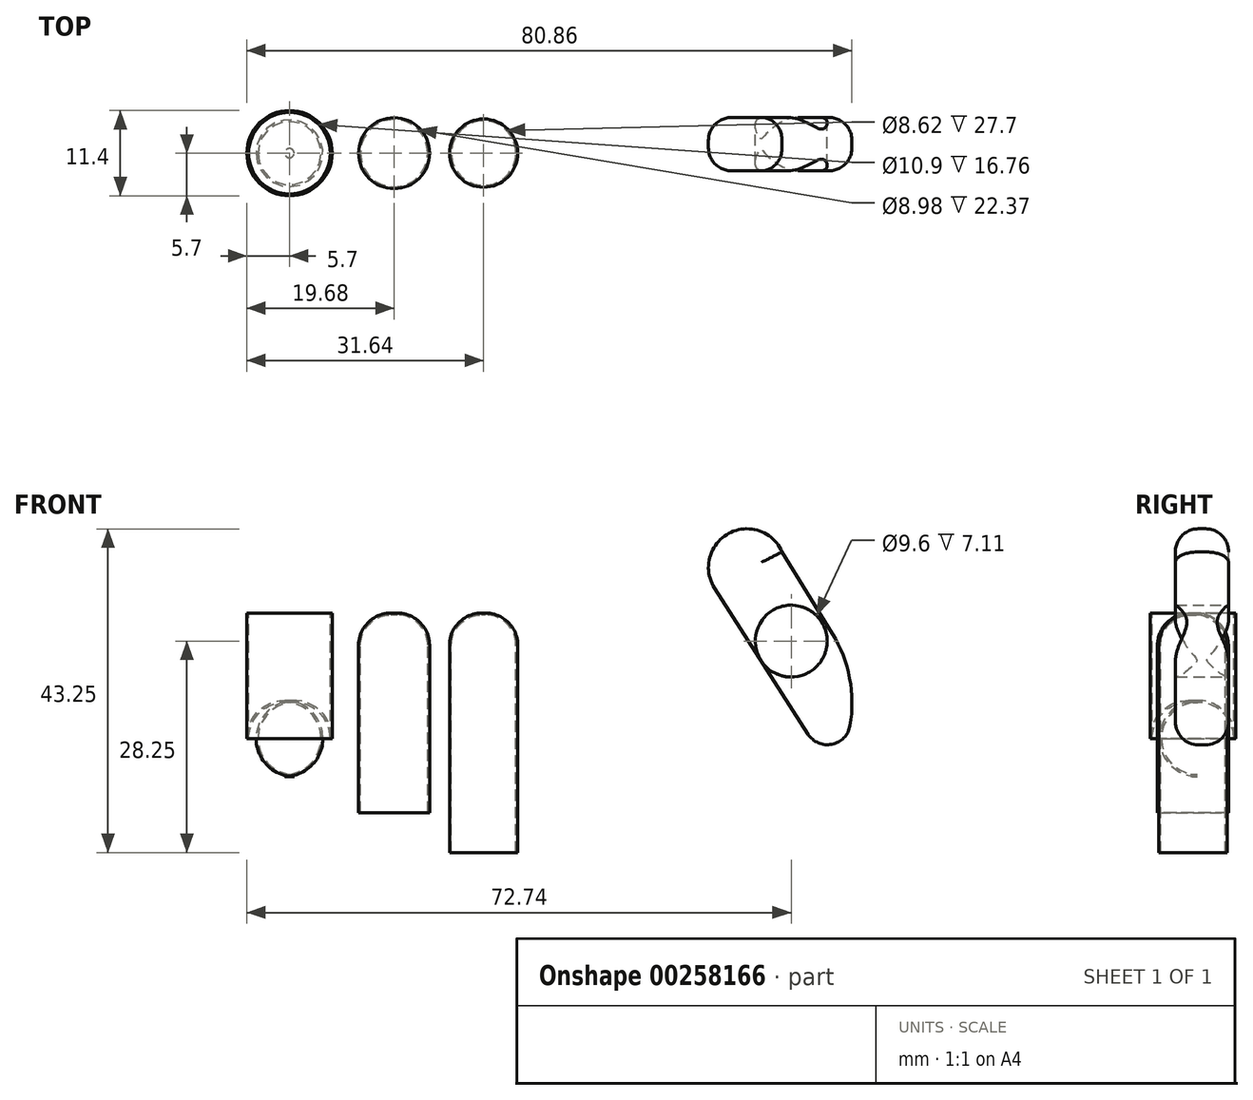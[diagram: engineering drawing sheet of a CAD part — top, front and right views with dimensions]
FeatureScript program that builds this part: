
annotation { "Feature Type Name" : "Feature", "Feature Type Description" : "" }
export const myFeature = defineFeature(function(context is Context, id is Id, definition is map)
    precondition{}
    {
        {
            var Q0;
            Q0=qCreatedBy(makeId("Front.planeOp"),FACE);
            var sketch = newSketch(context, id + "F0", { "sketchPlane" : qUnion([Q0])});
            skLineSegment(sketch, "E0", {"start": v(-7.79, 3.36) * mm, "end": v(7.96, -21.27) * mm});
            skLineSegment(sketch, "E1", {"start": v(7.96, -2.76) * mm, "end": v(1.24, 8.17) * mm});
            skArc(sketch, "E2", {"start": v(-7.79, 3.36) * mm, "mid": v(-5.88, 10.65) * mm, "end": v(1.24, 8.17) * mm});
            skCircle(sketch, "E3", {"center": v(2.46, -3.75) * mm, "radius": 4.8 * mm});
            skLineSegment(sketch, "E4", {"start": v(2.46, -3.75) * mm, "end": v(-1.63, -6.27) * mm});
            skLineSegment(sketch, "E5", {"start": v(-1.63, -6.27) * mm, "end": v(2.46, -3.75) * mm});
            skLineSegment(sketch, "E6", {"start": v(2.46, -3.75) * mm, "end": v(6.56, -1.23) * mm});
            skArc(sketch, "E7", {"start": v(7.96, -2.76) * mm, "mid": v(10.58, -12.01) * mm, "end": v(7.96, -21.27) * mm});
            skSolve(sketch);
        }
        {
            var Q0;
            {var subQ0=sQuery(id+"F0.wireOp",EDGE,"E5");Q0=makeQuery(id+"F0.imprint","IMPRINT",FACE,{"disambiguationData":[TD([[makeQuery(id+"F0.imprint","IMPRINT",EDGE,{"derivedFrom":subQ0}),-1.0]])]});}
            var Q1;
            {var subQ0=sQuery(id+"F0.wireOp",EDGE,"E5");Q1=makeQuery(id+"F0.imprint","IMPRINT",FACE,{"disambiguationData":[TD([[makeQuery(id+"F0.imprint","IMPRINT",EDGE,{"derivedFrom":subQ0}),1.0]])]});}
            var Q2;
            Q2=makeQuery(id+"F0.imprint","IMPRINT",FACE,{"disambiguationData":[TD([[makeQuery(id+"F0.imprint","IMPRINT",EDGE,{"derivedFrom":sQuery(id+"F0.wireOp",EDGE,"E1")}),1.0]])]});
            extrude(context, id + "F1", {"entities" : qUnion([Q0, Q1, Q2]), "depth" : 7.11 * mm});
        }
        {
            var Q0;
            Q0=makeQuery(id+"F1.opExtrude","CAP_EDGE",EDGE,{"disambiguationData":[OSD([sQuery(id+"F0.wireOp",EDGE,"E0")])],"isStart":true});
            var Q1;
            Q1=makeQuery(id+"F1.opExtrude","CAP_EDGE",EDGE,{"disambiguationData":[OSD([sQuery(id+"F0.wireOp",EDGE,"E2")])],"isStart":true});
            var Q2;
            Q2=makeQuery(id+"F1.opExtrude","CAP_EDGE",EDGE,{"disambiguationData":[OSD([sQuery(id+"F0.wireOp",EDGE,"E2")])],"isStart":false});
            var Q3;
            Q3=makeQuery(id+"F1.opExtrude","CAP_EDGE",EDGE,{"disambiguationData":[OSD([sQuery(id+"F0.wireOp",EDGE,"E0")])],"isStart":false});
            var Q4;
            Q4=makeQuery(id+"F1.opExtrude","CAP_EDGE",EDGE,{"disambiguationData":[OSD([sQuery(id+"F0.wireOp",EDGE,"E1")])],"isStart":true});
            var Q5;
            Q5=makeQuery(id+"F1.opExtrude","CAP_EDGE",EDGE,{"disambiguationData":[OSD([sQuery(id+"F0.wireOp",EDGE,"E7")])],"isStart":true});
            var Q6;
            Q6=makeQuery(id+"F1.opExtrude","SWEPT_EDGE",EDGE,{"disambiguationData":[OSD([sQuery(id+"F0.wireOp",EDGE,"E0"),sQuery(id+"F0.wireOp",EDGE,"E7")])]});
            var Q7;
            Q7=makeQuery(id+"F1.opExtrude","CAP_EDGE",EDGE,{"disambiguationData":[OSD([sQuery(id+"F0.wireOp",EDGE,"E1")])],"isStart":false});
            var Q8;
            Q8=makeQuery(id+"F1.opExtrude","CAP_EDGE",EDGE,{"disambiguationData":[OSD([sQuery(id+"F0.wireOp",EDGE,"E7")])],"isStart":false});
            fillet(context, id + "F2", {"entities" : qUnion([Q0, Q1, Q2, Q3, Q4, Q5, Q6, Q7, Q8]), "radius" : 3.07 * mm, "tangentPropagation" : true, "allowEdgeOverflow" : false});
        }
        {
            var Q0;
            Q0=qCreatedBy(makeId("Top.planeOp"),FACE);
            var sketch = newSketch(context, id + "F3", { "sketchPlane" : qUnion([Q0])});
            skCircle(sketch, "E8", {"center": v(-38.64, -4.76) * mm, "radius": 4.56 * mm});
            skCircle(sketch, "E9", {"center": v(-50.6, -4.76) * mm, "radius": 4.74 * mm});
            skCircle(sketch, "E10", {"center": v(-64.58, -4.76) * mm, "radius": 5.7 * mm});
            skSolve(sketch);
        }
        {
            var Q0;
            Q0=makeQuery(id+"F3.imprint","IMPRINT",FACE,{"disambiguationData":[TD([[makeQuery(id+"F3.imprint","IMPRINT",EDGE,{"derivedFrom":sQuery(id+"F3.wireOp",EDGE,"E8")}),1.0]])]});
            extrude(context, id + "F4", {"entities" : qUnion([Q0]), "oppositeDirection" : true, "depth" : 32 * mm});
        }
        {
            var Q0;
            Q0=makeQuery(id+"F4.opExtrude","CAP_EDGE",EDGE,{"disambiguationData":[OSD([sQuery(id+"F3.wireOp",EDGE,"E8")])],"isStart":true});
            fillet(context, id + "F5", {"entities" : qUnion([Q0]), "radius" : 4.3 * mm, "tangentPropagation" : true, "allowEdgeOverflow" : false});
        }
        {
            var Q0;
            Q0=makeQuery(id+"F4.opExtrude","CAP_FACE",FACE,{"disambiguationData":[OSD([sQuery(id+"F3.wireOp",EDGE,"E8")])],"isStart":false});
            shell(context, id + "F6", {"entities" : qUnion([Q0]), "thickness" : 0.25 * mm});
        }
        {
            var Q0;
            Q0=makeQuery(id+"F3.imprint","IMPRINT",FACE,{"disambiguationData":[TD([[makeQuery(id+"F3.imprint","IMPRINT",EDGE,{"derivedFrom":sQuery(id+"F3.wireOp",EDGE,"E9")}),1.0]])]});
            extrude(context, id + "F7", {"entities" : qUnion([Q0]), "oppositeDirection" : true, "depth" : 26.67 * mm});
        }
        {
            var Q0;
            Q0=makeQuery(id+"F7.opExtrude","CAP_EDGE",EDGE,{"disambiguationData":[OSD([sQuery(id+"F3.wireOp",EDGE,"E9")])],"isStart":true});
            fillet(context, id + "F8", {"entities" : qUnion([Q0]), "radius" : 4.3 * mm, "tangentPropagation" : true, "allowEdgeOverflow" : false});
        }
        {
            var Q0;
            Q0=makeQuery(id+"F7.opExtrude","CAP_FACE",FACE,{"disambiguationData":[OSD([sQuery(id+"F3.wireOp",EDGE,"E9")])],"isStart":false});
            shell(context, id + "F9", {"entities" : qUnion([Q0]), "thickness" : 0.25 * mm});
        }
        {
            var Q0;
            Q0=makeQuery(id+"F3.imprint","IMPRINT",FACE,{"disambiguationData":[TD([[makeQuery(id+"F3.imprint","IMPRINT",EDGE,{"derivedFrom":sQuery(id+"F3.wireOp",EDGE,"E10")}),1.0]])]});
            extrude(context, id + "F10", {"entities" : qUnion([Q0]), "oppositeDirection" : true, "depth" : 21.84 * mm});
        }
        {
            var Q0;
            Q0=makeQuery(id+"F10.opExtrude","CAP_EDGE",EDGE,{"disambiguationData":[OSD([sQuery(id+"F3.wireOp",EDGE,"E10")])],"isStart":false});
            fillet(context, id + "F11", {"entities" : qUnion([Q0]), "radius" : 5.08 * mm, "tangentPropagation" : true, "allowEdgeOverflow" : false});
        }
        {
            var Q0;
            Q0=makeQuery(id+"F10.opExtrude","CAP_FACE",FACE,{"disambiguationData":[OSD([sQuery(id+"F3.wireOp",EDGE,"E10")])],"isStart":true});
            shell(context, id + "F12", {"entities" : qUnion([Q0]), "thickness" : 0.25 * mm});
        }
    });
